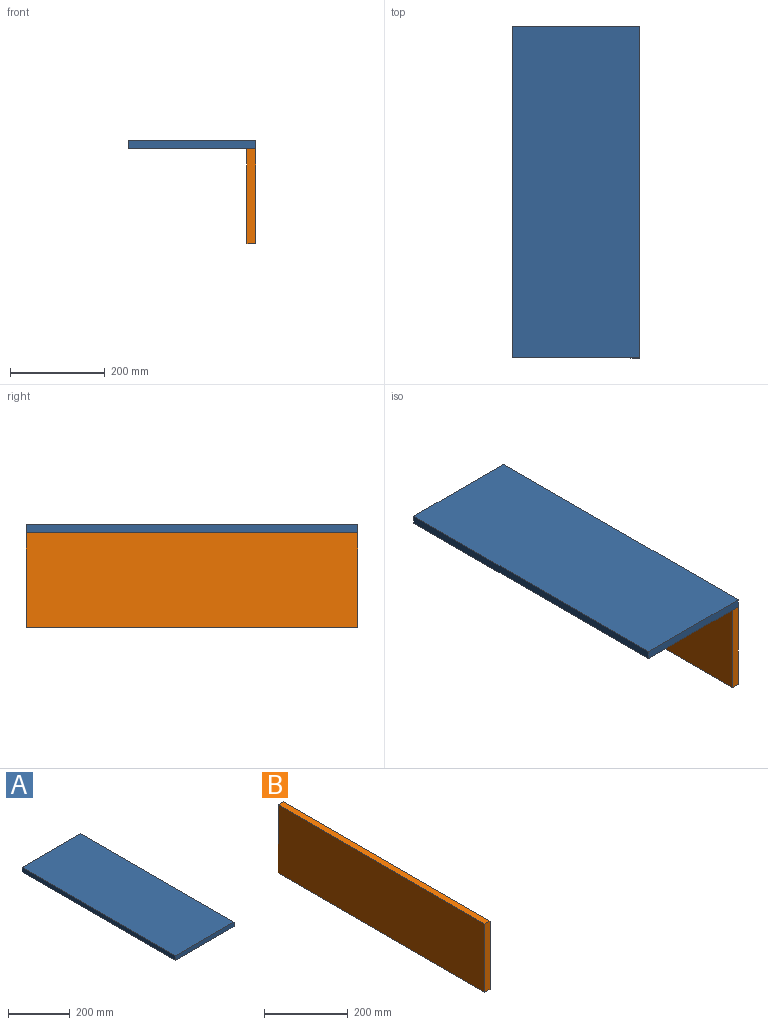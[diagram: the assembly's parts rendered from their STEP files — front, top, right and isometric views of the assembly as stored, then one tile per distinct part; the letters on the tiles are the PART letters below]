
ASSEMBLY  parts=2 mates=1
PART A: 6 faces, bbox 268x700x18 mm
  f0: plane 700x18mm, normal (-1,0,0), area 12600mm2, adj f1,f3,f4,f5
  f1: plane 268x18mm, normal (0,-1,0), area 4824mm2, adj f0,f2,f4,f5
  f2: plane 700x18mm, normal (1,0,0), area 12600mm2, adj f1,f3,f4,f5
  f3: plane 268x18mm, normal (0,1,0), area 4824mm2, adj f0,f2,f4,f5
  f4: plane 700x268mm, normal (0,0,1), area 187600mm2, adj f0,f1,f2,f3
  f5: plane 700x268mm, normal (0,0,-1), area 187600mm2, adj f0,f1,f2,f3
PART B: 6 faces, bbox 18x700x200 mm
  f0: plane 700x200mm, normal (-1,0,0), area 140000mm2, adj f1,f3,f4,f5
  f1: plane 200x18mm, normal (0,-1,0), area 3600mm2, adj f0,f2,f4,f5
  f2: plane 700x200mm, normal (1,0,0), area 140000mm2, adj f1,f3,f4,f5
  f3: plane 200x18mm, normal (0,1,0), area 3600mm2, adj f0,f2,f4,f5
  f4: plane 700x18mm, normal (0,0,1), area 12600mm2, adj f0,f1,f2,f3
  f5: plane 700x18mm, normal (0,0,-1), area 12600mm2, adj f0,f1,f2,f3
PLACE A t=(385.85,333.09,184.98)mm
PLACE B t=(3.89,13.38,-15.02)mm
MATE fastened A.f5 <-> B.f4  axis (0,0,-1) through (-1966.71,-1391.79,184.98)mm
